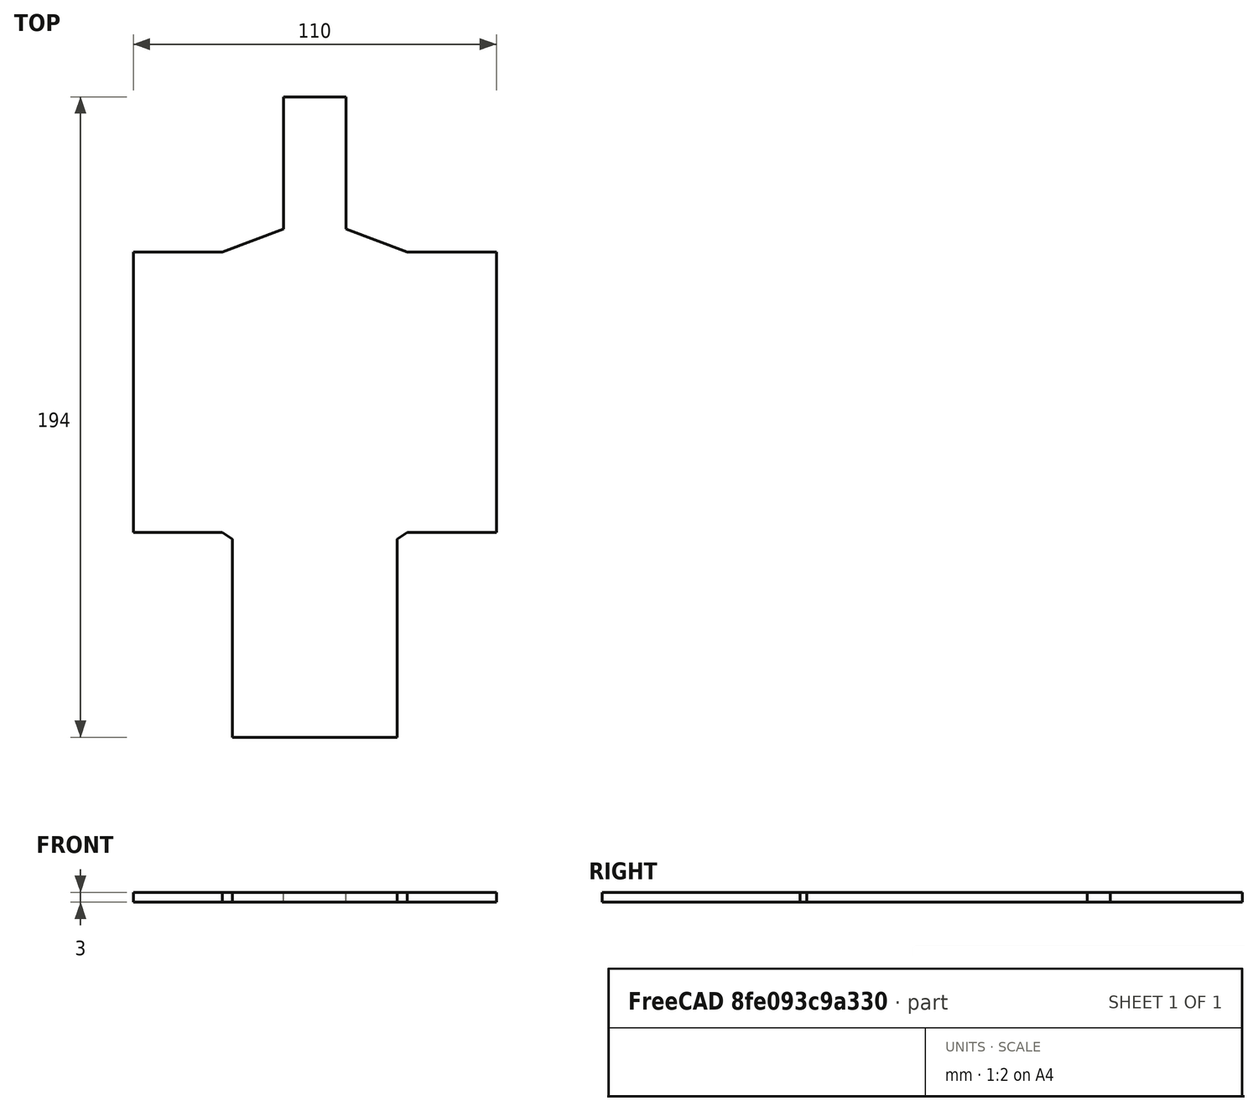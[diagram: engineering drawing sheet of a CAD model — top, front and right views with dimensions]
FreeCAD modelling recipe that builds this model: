
FCSTD DOCUMENT  (FreeCAD 0.20R29603 (Git))
Label: thesis cart platform
License: All rights reserved
LicenseURL: http://en.wikipedia.org/wiki/All_rights_reserved
objects: Sketcher::SketchObject×2, Part::Extrusion×2, PartDesign::Body×1, Part::FeaturePython×1
note: 6 computed .brp shape members not serialized (recipe doc carries the construction recipe); baked Part::Feature solids carry a one-line shape summary decoded from their .brp

FEATURE [Sketcher::SketchObject] Sketch
  FullyConstrained = true
  MapMode = 5
  Support = -> [XY_Plane]
  sketch-geometry (97):
    g0: LineSegment StartX=-55 StartY=-72.5 StartZ=0 EndX=-55 EndY=72.5 EndZ=0
    g1: LineSegment StartX=-55 StartY=72.5 StartZ=0 EndX=55 EndY=72.5 EndZ=0
    g2: LineSegment StartX=55 StartY=72.5 StartZ=0 EndX=55 EndY=-72.5 EndZ=0
    g3: LineSegment StartX=55 StartY=-72.5 StartZ=0 EndX=-55 EndY=-72.5 EndZ=0
    g4: GeomPoint X=0 Y=0 Z=0
    g5: LineSegment StartX=-55 StartY=-47.5 StartZ=0 EndX=-28 EndY=-47.5 EndZ=0
    g6: LineSegment StartX=-28 StartY=-47.5 StartZ=0 EndX=-28 EndY=-97.5 EndZ=0
    g7: LineSegment StartX=-28 StartY=-97.5 StartZ=0 EndX=-55 EndY=-97.5 EndZ=0
    g8: LineSegment StartX=-55 StartY=-97.5 StartZ=0 EndX=-55 EndY=-47.5 EndZ=0
    g9: LineSegment StartX=55 StartY=-47.5 StartZ=0 EndX=28 EndY=-47.5 EndZ=0
    g10: LineSegment StartX=28 StartY=-47.5 StartZ=0 EndX=28 EndY=-97.5 EndZ=0
    g11: LineSegment StartX=28 StartY=-97.5 StartZ=0 EndX=55 EndY=-97.5 EndZ=0
    g12: LineSegment StartX=55 StartY=-97.5 StartZ=0 EndX=55 EndY=-47.5 EndZ=0
    g13: LineSegment StartX=-55 StartY=47.5 StartZ=0 EndX=-28 EndY=47.5 EndZ=0
    g14: LineSegment StartX=-28 StartY=47.5 StartZ=0 EndX=-28 EndY=97.5 EndZ=0
    g15: LineSegment StartX=-28 StartY=97.5 StartZ=0 EndX=-55 EndY=97.5 EndZ=0
    g16: LineSegment StartX=-55 StartY=97.5 StartZ=0 EndX=-55 EndY=47.5 EndZ=0
    g17: LineSegment StartX=55 StartY=47.5 StartZ=0 EndX=28 EndY=47.5 EndZ=0
    g18: LineSegment StartX=55 StartY=97.5 StartZ=0 EndX=55 EndY=47.5 EndZ=0
    g19: LineSegment StartX=28 StartY=97.5 StartZ=0 EndX=55 EndY=97.5 EndZ=0
    g20: LineSegment StartX=28 StartY=47.5 StartZ=0 EndX=28 EndY=97.5 EndZ=0
    g21: LineSegment StartX=-7.5 StartY=72.5 StartZ=0 EndX=-7.5 EndY=84.5 EndZ=0
    g22: LineSegment StartX=-7.5 StartY=84.5 StartZ=0 EndX=7.5 EndY=84.5 EndZ=0
    g23: LineSegment StartX=7.5 StartY=84.5 StartZ=0 EndX=7.5 EndY=72.5 EndZ=0
    g24: LineSegment StartX=7.5 StartY=72.5 StartZ=0 EndX=-7.5 EndY=72.5 EndZ=0
    g25: GeomPoint X=0 Y=78.5 Z=0
    g26: LineSegment StartX=-7.5 StartY=72.5 StartZ=0 EndX=7.5 EndY=72.5 EndZ=0
    g27: LineSegment StartX=7.5 StartY=72.5 StartZ=0 EndX=7.5 EndY=60.5 EndZ=0
    g28: LineSegment StartX=7.5 StartY=60.5 StartZ=0 EndX=-7.5 EndY=60.5 EndZ=0
    g29: LineSegment StartX=-7.5 StartY=60.5 StartZ=0 EndX=-7.5 EndY=72.5 EndZ=0
    g30: Circle CenterX=-7.5 CenterY=84.5 CenterZ=0 NormalX=0 NormalY=0 NormalZ=1 AngleXU=0 Radius=1
    g31: Circle CenterX=7.5 CenterY=84.5 CenterZ=0 NormalX=0 NormalY=0 NormalZ=1 AngleXU=0 Radius=1
    g32: Circle CenterX=-7.5 CenterY=72.5 CenterZ=0 NormalX=0 NormalY=0 NormalZ=1 AngleXU=0 Radius=1
    g33: Circle CenterX=7.5 CenterY=72.5 CenterZ=0 NormalX=0 NormalY=0 NormalZ=1 AngleXU=0 Radius=1
    g34: Circle CenterX=7.5 CenterY=60.5 CenterZ=0 NormalX=0 NormalY=0 NormalZ=1 AngleXU=0 Radius=1
    g35: Circle CenterX=-7.5 CenterY=60.5 CenterZ=0 NormalX=0 NormalY=0 NormalZ=1 AngleXU=0 Radius=1
    g36: LineSegment StartX=-9.5 StartY=49.5 StartZ=0 EndX=-9.5 EndY=89.5 EndZ=0
    g37: LineSegment StartX=-9.5 StartY=89.5 StartZ=0 EndX=9.5 EndY=89.5 EndZ=0
    g38: LineSegment StartX=9.5 StartY=89.5 StartZ=0 EndX=9.5 EndY=49.5 EndZ=0
    g39: LineSegment StartX=9.5 StartY=49.5 StartZ=0 EndX=-9.5 EndY=49.5 EndZ=0
    g40: GeomPoint X=0 Y=69.5 Z=0
    g41: Circle CenterX=0 CenterY=40.5 CenterZ=0 NormalX=0 NormalY=0 NormalZ=1 AngleXU=0 Radius=7.5
    g42: LineSegment StartX=-3 StartY=30.5 StartZ=0 EndX=-3 EndY=40.5 EndZ=0
    g43: LineSegment StartX=-3 StartY=40.5 StartZ=0 EndX=3 EndY=40.5 EndZ=0
    g44: LineSegment StartX=3 StartY=40.5 StartZ=0 EndX=3 EndY=30.5 EndZ=0
    g45: LineSegment StartX=3 StartY=30.5 StartZ=0 EndX=-3 EndY=30.5 EndZ=0
    g46: GeomPoint X=0 Y=35.5 Z=0
    g47: LineSegment StartX=-21 StartY=-96 StartZ=0 EndX=-21 EndY=-49 EndZ=0
    g48: LineSegment StartX=-21 StartY=-49 StartZ=0 EndX=21 EndY=-49 EndZ=0
    g49: LineSegment StartX=21 StartY=-49 StartZ=0 EndX=21 EndY=-96 EndZ=0
    g50: LineSegment StartX=21 StartY=-96 StartZ=0 EndX=-21 EndY=-96 EndZ=0
    g51: GeomPoint X=0 Y=-72.5 Z=0
    g52: GeomPoint X=-16 Y=-96 Z=0
    g53: GeomPoint X=16 Y=-96 Z=0
    g54: GeomPoint X=16 Y=-49 Z=0
    g55: GeomPoint X=-16 Y=-49 Z=0
    g56: Circle CenterX=-21 CenterY=-49 CenterZ=0 NormalX=0 NormalY=0 NormalZ=1 AngleXU=0 Radius=0.75
    g57: Circle CenterX=-16 CenterY=-49 CenterZ=0 NormalX=0 NormalY=0 NormalZ=1 AngleXU=0 Radius=0.75
    g58: Circle CenterX=16 CenterY=-49 CenterZ=0 NormalX=0 NormalY=0 NormalZ=1 AngleXU=0 Radius=0.75
    g59: Circle CenterX=21 CenterY=-49 CenterZ=0 NormalX=0 NormalY=0 NormalZ=1 AngleXU=0 Radius=0.75
    g60: Circle CenterX=-21 CenterY=-96 CenterZ=0 NormalX=0 NormalY=0 NormalZ=1 AngleXU=0 Radius=0.75
    g61: Circle CenterX=-16 CenterY=-96 CenterZ=0 NormalX=0 NormalY=0 NormalZ=1 AngleXU=0 Radius=0.75
    g62: Circle CenterX=16 CenterY=-96 CenterZ=0 NormalX=0 NormalY=0 NormalZ=1 AngleXU=0 Radius=0.75
    g63: Circle CenterX=21 CenterY=-96 CenterZ=0 NormalX=0 NormalY=0 NormalZ=1 AngleXU=0 Radius=0.75
    g64: LineSegment StartX=-25 StartY=-104.5 StartZ=0 EndX=-25 EndY=-44.5 EndZ=0
    g65: LineSegment StartX=-25 StartY=-44.5 StartZ=0 EndX=25 EndY=-44.5 EndZ=0
    g66: LineSegment StartX=25 StartY=-44.5 StartZ=0 EndX=25 EndY=-104.5 EndZ=0
    g67: LineSegment StartX=25 StartY=-104.5 StartZ=0 EndX=-25 EndY=-104.5 EndZ=0
    g68: GeomPoint X=0 Y=-74.5 Z=0
    g69: LineSegment StartX=-2.5 StartY=-92.5 StartZ=0 EndX=-2.5 EndY=-52.5 EndZ=0
    g70: LineSegment StartX=-2.5 StartY=-52.5 StartZ=0 EndX=12.5 EndY=-52.5 EndZ=0
    g71: LineSegment StartX=12.5 StartY=-52.5 StartZ=0 EndX=12.5 EndY=-92.5 EndZ=0
    g72: LineSegment StartX=12.5 StartY=-92.5 StartZ=0 EndX=-2.5 EndY=-92.5 EndZ=0
    g73: GeomPoint X=5 Y=-72.5 Z=0
    g74: LineSegment StartX=-25 StartY=-86 StartZ=0 EndX=-25 EndY=-59 EndZ=0
    g75: LineSegment StartX=-25 StartY=-59 StartZ=0 EndX=-12 EndY=-59 EndZ=0
    g76: LineSegment StartX=-12 StartY=-59 StartZ=0 EndX=-12 EndY=-86 EndZ=0
    g77: LineSegment StartX=-12 StartY=-86 StartZ=0 EndX=-25 EndY=-86 EndZ=0
    g78: GeomPoint X=-18.5 Y=-72.5 Z=0
    g79: LineSegment StartX=12 StartY=-86 StartZ=0 EndX=12 EndY=-59 EndZ=0
    g80: LineSegment StartX=12 StartY=-59 StartZ=0 EndX=25 EndY=-59 EndZ=0
    g81: LineSegment StartX=25 StartY=-59 StartZ=0 EndX=25 EndY=-86 EndZ=0
    g82: LineSegment StartX=25 StartY=-86 StartZ=0 EndX=12 EndY=-86 EndZ=0
    g83: GeomPoint X=18.5 Y=-72.5 Z=0
    g84: LineSegment StartX=-55 StartY=-42.5 StartZ=0 EndX=-55 EndY=42.5 EndZ=0
    g85: LineSegment StartX=-55 StartY=42.5 StartZ=0 EndX=55 EndY=42.5 EndZ=0
    g86: LineSegment StartX=55 StartY=42.5 StartZ=0 EndX=55 EndY=-42.5 EndZ=0
    g87: LineSegment StartX=55 StartY=-42.5 StartZ=0 EndX=-55 EndY=-42.5 EndZ=0
    g88: GeomPoint X=0 Y=1.8e-15 Z=0
    g89: LineSegment StartX=55 StartY=42.5 StartZ=0 EndX=28 EndY=42.5 EndZ=0
    g90: LineSegment StartX=-55 StartY=42.5 StartZ=0 EndX=-28 EndY=42.5 EndZ=0
    g91: LineSegment StartX=-55 StartY=-42.5 StartZ=0 EndX=-28 EndY=-42.5 EndZ=0
    g92: LineSegment StartX=55 StartY=-42.5 StartZ=0 EndX=28 EndY=-42.5 EndZ=0
    g93: LineSegment StartX=-28 StartY=-42.5 StartZ=0 EndX=-25 EndY=-44.5 EndZ=0
    g94: LineSegment StartX=25 StartY=-44.5 StartZ=0 EndX=28 EndY=-42.5 EndZ=0
    g95: LineSegment StartX=28 StartY=42.5 StartZ=0 EndX=9.5 EndY=49.5 EndZ=0
    g96: LineSegment StartX=-28 StartY=42.5 StartZ=0 EndX=-9.5 EndY=49.5 EndZ=0
  constraints (237):
    c: Coincident(g0,g1)
    c: Coincident(g1,g2)
    c: Coincident(g2,g3)
    c: Coincident(g3,g0)
    c: Horizontal(g1)
    c: Horizontal(g3)
    c: Vertical(g0)
    c: Vertical(g2)
    c: Symmetric(g1,g0,g4)
    c: Coincident(g4,g-1)
    c: DistanceX(g1,g1) = 110
    c: DistanceY(g0,g0) = 145
    c: Coincident(g5,g6)
    c: Coincident(g6,g7)
    c: Coincident(g7,g8)
    c: Coincident(g8,g5)
    c: Horizontal(g5)
    c: Horizontal(g7)
    c: Vertical(g6)
    c: Vertical(g8)
    c: PointOnObject(g5,g0)
    c: DistanceY(g8,g8) = 50  'wheeldiam'
    c: DistanceX(g5,g5) = 27  'wheelwidth'
    c: Distance(g5,g0) = 25
    c: Coincident(g9,g10)
    c: Coincident(g10,g11)
    c: Coincident(g11,g12)
    c: Coincident(g12,g9)
    c: Horizontal(g9)
    c: Horizontal(g11)
    c: Vertical(g10)
    c: Vertical(g12)
    c: Coincident(g13,g14)
    c: Coincident(g14,g15)
    c: Coincident(g15,g16)
    c: Coincident(g16,g13)
    c: Horizontal(g13)
    c: Horizontal(g15)
    c: Vertical(g14)
    c: Vertical(g16)
    c: Coincident(g17,g20)
    c: Coincident(g20,g19)
    c: Coincident(g19,g18)
    c: Coincident(g18,g17)
    c: Horizontal(g17)
    c: Horizontal(g19)
    c: Vertical(g20)
    c: Vertical(g18)
    c: Equal(g11,g5)
    c: Equal(g6,g10)
    c: Equal(g6,g14)
    c: Equal(g5,g13)
    c: Equal(g6,g20)
    c: Equal(g5,g17)
    c: PointOnObject(g13,g0)
    c: PointOnObject(g17,g2)
    c: PointOnObject(g9,g2)
    c: Distance(g11,g2) = 25
    c: Distance(g17,g1) = 25
    c: Distance(g13,g0) = 25
    c: Coincident(g21,g22)
    c: Coincident(g22,g23)
    c: Coincident(g23,g24)
    c: Coincident(g24,g21)
    c: Horizontal(g22)
    c: Horizontal(g24)
    c: Vertical(g21)
    c: Vertical(g23)
    c: Symmetric(g22,g21,g25)
    c: Distance(g22) = 15
    c: Distance(g23) = 12
    c: Coincident(g26,g27)
    c: Coincident(g27,g28)
    c: Coincident(g28,g29)
    c: Coincident(g29,g26)
    c: Horizontal(g26)
    c: Horizontal(g28)
    c: Vertical(g27)
    c: Vertical(g29)
    c: Coincident(g26,g21)
    c: PointOnObject(g23,g27)
    c: Distance(g27) = 12
    c: PointOnObject(g21,g1)
    c: PointOnObject(g25,g-2)
    c: Coincident(g30,g21)
    c: Coincident(g31,g22)
    c: Coincident(g32,g21)
    c: Coincident(g33,g23)
    c: Coincident(g34,g27)
    c: Coincident(g35,g28)
    c: Equal(g30, g31-g35) x5
    c: Radius(g30) = 1
    c: Coincident(g36,g37)
    c: Coincident(g37,g38)
    c: Coincident(g38,g39)
    c: Coincident(g39,g36)
    c: Horizontal(g37)
    c: Horizontal(g39)
    c: Vertical(g36)
    c: Vertical(g38)
    c: Symmetric(g37,g36,g40)
    c: Distance(g37) = 19
    c: Distance(g38) = 40
    c: PointOnObject(g40,g-2)
    c: DistanceY(g30,g36) = 5
    c: Diameter(g41) = 15
    c: DistanceY(g41,g0) = 32
    c: PointOnObject(g41,g-2)
    c: Coincident(g42,g43)
    c: Coincident(g43,g44)
    c: Coincident(g44,g45)
    c: Coincident(g45,g42)
    c: Horizontal(g43)
    c: Horizontal(g45)
    c: Vertical(g42)
    c: Vertical(g44)
    c: Symmetric(g43,g42,g46)
    c: Horizontal(g42,g41)
    c: Distance(g43) = 6
    c: Distance(g42) = 10
    c: PointOnObject(g46,g-2)
    c: Coincident(g47,g48)
    c: Coincident(g48,g49)
    c: Coincident(g49,g50)
    c: Coincident(g50,g47)
    c: Horizontal(g48)
    c: Horizontal(g50)
    c: Vertical(g47)
    c: Vertical(g49)
    c: Symmetric(g48,g47,g51)
    c: DistanceX(g50,g50) = 42
    c: PointOnObject(g52,g50)
    c: PointOnObject(g53,g50)
    c: PointOnObject(g54,g48)
    c: PointOnObject(g55,g48)
    c: Vertical(g55,g52)
    c: Vertical(g54,g53)
    c: DistanceX(g47,g52) = 5
    c: DistanceX(g53,g49) = 5
    c: DistanceY(g47,g47) = 47
    c: PointOnObject(g51,g3)
    c: PointOnObject(g51,g-2)
    c: Coincident(g56,g47)
    c: Coincident(g57,g55)
    c: Coincident(g58,g54)
    c: Coincident(g59,g48)
    c: Coincident(g60,g47)
    c: Coincident(g61,g52)
    c: Coincident(g62,g53)
    c: Coincident(g63,g49)
    c: Equal(g56, g57-g63) x7
    c: Diameter(g56) = 1.5
    c: Coincident(g64,g65)
    c: Coincident(g65,g66)
    c: Coincident(g66,g67)
    c: Coincident(g67,g64)
    c: Horizontal(g65)
    c: Horizontal(g67)
    c: Vertical(g64)
    c: Vertical(g66)
    c: Symmetric(g65,g64,g68)
    c: DistanceX(g67,g67) = 50
    c: DistanceY(g64,g64) = 60
    c: DistanceY(g68,g5) = 27
    c: PointOnObject(g68,g-2)
    c: Coincident(g69,g70)
    c: Coincident(g70,g71)
    c: Coincident(g71,g72)
    c: Coincident(g72,g69)
    c: Horizontal(g70)
    c: Horizontal(g72)
    c: Vertical(g69)
    c: Vertical(g71)
    c: Symmetric(g70,g69,g73)
    c: DistanceY(g69,g69) = 40
    c: DistanceX(g72,g72) = 15
    c: PointOnObject(g73,g3)
    c: DistanceX(g73,g66) = 20
    c: Coincident(g74,g75)
    c: Coincident(g75,g76)
    c: Coincident(g76,g77)
    c: Coincident(g77,g74)
    c: Horizontal(g75)
    c: Horizontal(g77)
    c: Vertical(g74)
    c: Vertical(g76)
    c: Symmetric(g75,g74,g78)
    c: DistanceX(g77,g77) = 13
    c: DistanceY(g74,g74) = 27
    c: PointOnObject(g78,g3)
    c: Coincident(g79,g80)
    c: Coincident(g80,g81)
    c: Coincident(g81,g82)
    c: Coincident(g82,g79)
    c: Horizontal(g80)
    c: Horizontal(g82)
    c: Vertical(g79)
    c: Vertical(g81)
    c: Symmetric(g80,g79,g83)
    c: DistanceX(g82,g82) = 13
    c: DistanceY(g79,g79) = 27
    c: PointOnObject(g83,g3)
    c: PointOnObject(g74,g64)
    c: PointOnObject(g80,g66)
    c: Coincident(g84,g85)
    c: Coincident(g85,g86)
    c: Coincident(g86,g87)
    c: Coincident(g87,g84)
    c: Horizontal(g85)
    c: Horizontal(g87)
    c: Vertical(g84)
    c: Vertical(g86)
    c: Symmetric(g85,g84,g88)
    c: PointOnObject(g84,g0)
    c: PointOnObject(g88,g-2)
    c: DistanceY(g85,g17) = 5
    c: DistanceY(g9,g86) = 5
    c: Coincident(g89,g86)
    c: Coincident(g90,g84)
    c: Coincident(g91,g84)
    c: Coincident(g92,g86)
    c: Vertical(g89,g92)
    c: Vertical(g91,g90)
    c: Horizontal(g90,g89)
    c: Horizontal(g92,g91)
    c: Vertical(g90,g13)
    c: Vertical(g89,g17)
    c: PointOnObject(g89,g85)
    c: PointOnObject(g92,g87)
    c: Coincident(g93,g91)
    c: Coincident(g93,g64)
    c: Coincident(g94,g66)
    c: Coincident(g94,g92)
    c: Coincident(g95,g89)
    c: Coincident(g95,g38)
    c: Coincident(g96,g90)
    c: Coincident(g96,g36)
FEATURE [PartDesign::Body] Body
  Group = -> [Sketch]
  Origin = -> Origin
FEATURE [Sketcher::SketchObject] Sketch001
  FullyConstrained = true
  MapMode = 5
  Support = -> [XY_Plane001]
  sketch-geometry (236):
    g0: LineSegment StartX=-55 StartY=-72.5 StartZ=0 EndX=-55 EndY=72.5 EndZ=0
    g1: LineSegment StartX=-55 StartY=72.5 StartZ=0 EndX=55 EndY=72.5 EndZ=0
    g2: LineSegment StartX=55 StartY=72.5 StartZ=0 EndX=55 EndY=-72.5 EndZ=0
    g3: LineSegment StartX=55 StartY=-72.5 StartZ=0 EndX=-55 EndY=-72.5 EndZ=0
    g4: GeomPoint X=0 Y=0 Z=0
    g5: LineSegment StartX=-55 StartY=-47.5 StartZ=0 EndX=-28 EndY=-47.5 EndZ=0
    g6: LineSegment StartX=-28 StartY=-47.5 StartZ=0 EndX=-28 EndY=-97.5 EndZ=0
    g7: LineSegment StartX=-28 StartY=-97.5 StartZ=0 EndX=-55 EndY=-97.5 EndZ=0
    g8: LineSegment StartX=-55 StartY=-97.5 StartZ=0 EndX=-55 EndY=-47.5 EndZ=0
    g9: LineSegment StartX=55 StartY=-47.5 StartZ=0 EndX=28 EndY=-47.5 EndZ=0
    g10: LineSegment StartX=28 StartY=-47.5 StartZ=0 EndX=28 EndY=-97.5 EndZ=0
    g11: LineSegment StartX=28 StartY=-97.5 StartZ=0 EndX=55 EndY=-97.5 EndZ=0
    g12: LineSegment StartX=55 StartY=-97.5 StartZ=0 EndX=55 EndY=-47.5 EndZ=0
    g13: LineSegment StartX=-55 StartY=47.5 StartZ=0 EndX=-28 EndY=47.5 EndZ=0
    g14: LineSegment StartX=-28 StartY=47.5 StartZ=0 EndX=-28 EndY=97.5 EndZ=0
    g15: LineSegment StartX=-28 StartY=97.5 StartZ=0 EndX=-55 EndY=97.5 EndZ=0
    g16: LineSegment StartX=-55 StartY=97.5 StartZ=0 EndX=-55 EndY=47.5 EndZ=0
    g17: LineSegment StartX=55 StartY=47.5 StartZ=0 EndX=28 EndY=47.5 EndZ=0
    g18: LineSegment StartX=55 StartY=97.5 StartZ=0 EndX=55 EndY=47.5 EndZ=0
    g19: LineSegment StartX=28 StartY=97.5 StartZ=0 EndX=55 EndY=97.5 EndZ=0
    g20: LineSegment StartX=28 StartY=47.5 StartZ=0 EndX=28 EndY=97.5 EndZ=0
    g21: LineSegment StartX=-7.5 StartY=72.5 StartZ=0 EndX=-7.5 EndY=84.5 EndZ=0
    g22: LineSegment StartX=-7.5 StartY=84.5 StartZ=0 EndX=7.5 EndY=84.5 EndZ=0
    g23: LineSegment StartX=7.5 StartY=84.5 StartZ=0 EndX=7.5 EndY=72.5 EndZ=0
    g24: LineSegment StartX=7.5 StartY=72.5 StartZ=0 EndX=-7.5 EndY=72.5 EndZ=0
    g25: GeomPoint X=0 Y=78.5 Z=0
    g26: LineSegment StartX=-7.5 StartY=72.5 StartZ=0 EndX=7.5 EndY=72.5 EndZ=0
    g27: LineSegment StartX=7.5 StartY=72.5 StartZ=0 EndX=7.5 EndY=60.5 EndZ=0
    g28: LineSegment StartX=7.5 StartY=60.5 StartZ=0 EndX=-7.5 EndY=60.5 EndZ=0
    g29: LineSegment StartX=-7.5 StartY=60.5 StartZ=0 EndX=-7.5 EndY=72.5 EndZ=0
    g30: Circle CenterX=-7.5 CenterY=84.5 CenterZ=0 NormalX=0 NormalY=0 NormalZ=1 AngleXU=0 Radius=1
    g31: Circle CenterX=7.5 CenterY=84.5 CenterZ=0 NormalX=0 NormalY=0 NormalZ=1 AngleXU=0 Radius=1
    g32: Circle CenterX=-7.5 CenterY=72.5 CenterZ=0 NormalX=0 NormalY=0 NormalZ=1 AngleXU=0 Radius=1
    g33: Circle CenterX=7.5 CenterY=72.5 CenterZ=0 NormalX=0 NormalY=0 NormalZ=1 AngleXU=0 Radius=1
    g34: Circle CenterX=7.5 CenterY=60.5 CenterZ=0 NormalX=0 NormalY=0 NormalZ=1 AngleXU=0 Radius=1
    g35: Circle CenterX=-7.5 CenterY=60.5 CenterZ=0 NormalX=0 NormalY=0 NormalZ=1 AngleXU=0 Radius=1
    g36: LineSegment StartX=-9.5 StartY=49.5 StartZ=0 EndX=-9.5 EndY=89.5 EndZ=0
    g37: LineSegment StartX=-9.5 StartY=89.5 StartZ=0 EndX=9.5 EndY=89.5 EndZ=0
    g38: LineSegment StartX=9.5 StartY=89.5 StartZ=0 EndX=9.5 EndY=49.5 EndZ=0
    g39: LineSegment StartX=9.5 StartY=49.5 StartZ=0 EndX=-9.5 EndY=49.5 EndZ=0
    g40: GeomPoint X=0 Y=69.5 Z=0
    g41: Circle CenterX=0 CenterY=40.5 CenterZ=0 NormalX=0 NormalY=0 NormalZ=1 AngleXU=0 Radius=7.5
    g42: LineSegment StartX=-3 StartY=30.5 StartZ=0 EndX=-3 EndY=40.5 EndZ=0
    g43: LineSegment StartX=-3 StartY=40.5 StartZ=0 EndX=3 EndY=40.5 EndZ=0
    g44: LineSegment StartX=3 StartY=40.5 StartZ=0 EndX=3 EndY=30.5 EndZ=0
    g45: LineSegment StartX=3 StartY=30.5 StartZ=0 EndX=-3 EndY=30.5 EndZ=0
    g46: GeomPoint X=0 Y=35.5 Z=0
    g47: LineSegment StartX=-21 StartY=-96 StartZ=0 EndX=-21 EndY=-49 EndZ=0
    g48: LineSegment StartX=-21 StartY=-49 StartZ=0 EndX=21 EndY=-49 EndZ=0
    g49: LineSegment StartX=21 StartY=-49 StartZ=0 EndX=21 EndY=-96 EndZ=0
    g50: LineSegment StartX=21 StartY=-96 StartZ=0 EndX=-21 EndY=-96 EndZ=0
    g51: GeomPoint X=0 Y=-72.5 Z=0
    g52: GeomPoint X=-16 Y=-96 Z=0
    g53: GeomPoint X=16 Y=-96 Z=0
    g54: GeomPoint X=16 Y=-49 Z=0
    g55: GeomPoint X=-16 Y=-49 Z=0
    g56: Circle CenterX=-21 CenterY=-49 CenterZ=0 NormalX=0 NormalY=0 NormalZ=1 AngleXU=0 Radius=0.75
    g57: Circle CenterX=-16 CenterY=-49 CenterZ=0 NormalX=0 NormalY=0 NormalZ=1 AngleXU=0 Radius=0.75
    g58: Circle CenterX=16 CenterY=-49 CenterZ=0 NormalX=0 NormalY=0 NormalZ=1 AngleXU=0 Radius=0.75
    g59: Circle CenterX=21 CenterY=-49 CenterZ=0 NormalX=0 NormalY=0 NormalZ=1 AngleXU=0 Radius=0.75
    g60: Circle CenterX=-21 CenterY=-96 CenterZ=0 NormalX=0 NormalY=0 NormalZ=1 AngleXU=0 Radius=0.75
    g61: Circle CenterX=-16 CenterY=-96 CenterZ=0 NormalX=0 NormalY=0 NormalZ=1 AngleXU=0 Radius=0.75
    g62: Circle CenterX=16 CenterY=-96 CenterZ=0 NormalX=0 NormalY=0 NormalZ=1 AngleXU=0 Radius=0.75
    g63: Circle CenterX=21 CenterY=-96 CenterZ=0 NormalX=0 NormalY=0 NormalZ=1 AngleXU=0 Radius=0.75
    g64: LineSegment StartX=-25 StartY=-104.5 StartZ=0 EndX=-25 EndY=-44.5 EndZ=0
    g65: LineSegment StartX=-25 StartY=-44.5 StartZ=0 EndX=25 EndY=-44.5 EndZ=0
    g66: LineSegment StartX=25 StartY=-44.5 StartZ=0 EndX=25 EndY=-104.5 EndZ=0
    g67: LineSegment StartX=25 StartY=-104.5 StartZ=0 EndX=-25 EndY=-104.5 EndZ=0
    g68: GeomPoint X=0 Y=-74.5 Z=0
    g69: LineSegment StartX=-2.5 StartY=-92.5 StartZ=0 EndX=-2.5 EndY=-52.5 EndZ=0
    g70: LineSegment StartX=-2.5 StartY=-52.5 StartZ=0 EndX=12.5 EndY=-52.5 EndZ=0
    g71: LineSegment StartX=12.5 StartY=-52.5 StartZ=0 EndX=12.5 EndY=-92.5 EndZ=0
    g72: LineSegment StartX=12.5 StartY=-92.5 StartZ=0 EndX=-2.5 EndY=-92.5 EndZ=0
    g73: GeomPoint X=5 Y=-72.5 Z=0
    g74: LineSegment StartX=-25 StartY=-86 StartZ=0 EndX=-25 EndY=-59 EndZ=0
    g75: LineSegment StartX=-25 StartY=-59 StartZ=0 EndX=-12 EndY=-59 EndZ=0
    g76: LineSegment StartX=-12 StartY=-59 StartZ=0 EndX=-12 EndY=-86 EndZ=0
    g77: LineSegment StartX=-12 StartY=-86 StartZ=0 EndX=-25 EndY=-86 EndZ=0
    g78: GeomPoint X=-18.5 Y=-72.5 Z=0
    g79: LineSegment StartX=12 StartY=-86 StartZ=0 EndX=12 EndY=-59 EndZ=0
    g80: LineSegment StartX=12 StartY=-59 StartZ=0 EndX=25 EndY=-59 EndZ=0
    g81: LineSegment StartX=25 StartY=-59 StartZ=0 EndX=25 EndY=-86 EndZ=0
    g82: LineSegment StartX=25 StartY=-86 StartZ=0 EndX=12 EndY=-86 EndZ=0
    g83: GeomPoint X=18.5 Y=-72.5 Z=0
    g84: LineSegment StartX=-55 StartY=-42.5 StartZ=0 EndX=-55 EndY=42.5 EndZ=0
    g85: LineSegment StartX=-55 StartY=42.5 StartZ=0 EndX=55 EndY=42.5 EndZ=0
    g86: LineSegment StartX=55 StartY=42.5 StartZ=0 EndX=55 EndY=-42.5 EndZ=0
    g87: LineSegment StartX=55 StartY=-42.5 StartZ=0 EndX=-55 EndY=-42.5 EndZ=0
    g88: GeomPoint X=0 Y=2.4e-15 Z=0
    g89: LineSegment StartX=55 StartY=42.5 StartZ=0 EndX=28 EndY=42.5 EndZ=0
    g90: LineSegment StartX=-55 StartY=42.5 StartZ=0 EndX=-28 EndY=42.5 EndZ=0
    g91: LineSegment StartX=-55 StartY=-42.5 StartZ=0 EndX=-28 EndY=-42.5 EndZ=0
    g92: LineSegment StartX=55 StartY=-42.5 StartZ=0 EndX=28 EndY=-42.5 EndZ=0
    g93: LineSegment StartX=-28 StartY=-42.5 StartZ=0 EndX=-25 EndY=-44.5 EndZ=0
    g94: LineSegment StartX=25 StartY=-44.5 StartZ=0 EndX=28 EndY=-42.5 EndZ=0
    g95: LineSegment StartX=28 StartY=42.5 StartZ=0 EndX=9.5 EndY=49.5 EndZ=0
    g96: LineSegment StartX=-28 StartY=42.5 StartZ=0 EndX=-9.5 EndY=49.5 EndZ=0
    g97: Circle CenterX=-21 CenterY=-26 CenterZ=0 NormalX=0 NormalY=0 NormalZ=1 AngleXU=0 Radius=1
    g98: Circle CenterX=-16 CenterY=-26 CenterZ=0 NormalX=0 NormalY=0 NormalZ=1 AngleXU=0 Radius=1
    g99: Circle CenterX=16 CenterY=-26 CenterZ=0 NormalX=0 NormalY=0 NormalZ=1 AngleXU=0 Radius=1
    g100: Circle CenterX=21 CenterY=-26 CenterZ=0 NormalX=0 NormalY=0 NormalZ=1 AngleXU=0 Radius=1
    g101: Circle CenterX=-21 CenterY=-3 CenterZ=0 NormalX=0 NormalY=0 NormalZ=1 AngleXU=0 Radius=1
    g102: Circle CenterX=-16 CenterY=-3 CenterZ=0 NormalX=0 NormalY=0 NormalZ=1 AngleXU=0 Radius=1
    g103: Circle CenterX=16 CenterY=-3 CenterZ=0 NormalX=0 NormalY=0 NormalZ=1 AngleXU=0 Radius=1
    g104: Circle CenterX=21 CenterY=-3 CenterZ=0 NormalX=0 NormalY=0 NormalZ=1 AngleXU=0 Radius=1
    g105: LineSegment StartX=36 StartY=-39.1 StartZ=0 EndX=36 EndY=-5.9 EndZ=0
    g106: LineSegment StartX=36.9 StartY=-5 StartZ=0 EndX=37.1 EndY=-5 EndZ=0
    g107: LineSegment StartX=38 StartY=-5.9 StartZ=0 EndX=38 EndY=-39.1 EndZ=0
    g108: LineSegment StartX=37.1 StartY=-40 StartZ=0 EndX=36.9 EndY=-40 EndZ=0
    g109: GeomPoint X=37 Y=-22.5 Z=0
    g110: LineSegment StartX=30 StartY=-39.1 StartZ=0 EndX=30 EndY=-5.9 EndZ=0
    g111: LineSegment StartX=30.9 StartY=-5 StartZ=0 EndX=31.1 EndY=-5 EndZ=0
    g112: LineSegment StartX=32 StartY=-5.9 StartZ=0 EndX=32 EndY=-39.1 EndZ=0
    g113: LineSegment StartX=31.1 StartY=-40 StartZ=0 EndX=30.9 EndY=-40 EndZ=0
    g114: GeomPoint X=31 Y=-22.5 Z=0
    g115: ArcOfCircle CenterX=30.9 CenterY=-5.9 CenterZ=0 NormalX=0 NormalY=0 NormalZ=1 AngleXU=0 Radius=0.9 StartAngle=1.5708 EndAngle=3.14159
    g116: GeomPoint X=30 Y=-5 Z=0
    g117: ArcOfCircle CenterX=31.1 CenterY=-5.9 CenterZ=0 NormalX=0 NormalY=0 NormalZ=1 AngleXU=0 Radius=0.9 StartAngle=0 EndAngle=1.5708
    g118: GeomPoint X=32 Y=-5 Z=0
    g119: ArcOfCircle CenterX=36.9 CenterY=-5.9 CenterZ=0 NormalX=0 NormalY=0 NormalZ=1 AngleXU=0 Radius=0.9 StartAngle=1.5708 EndAngle=3.14159
    g120: GeomPoint X=36 Y=-5 Z=0
    g121: ArcOfCircle CenterX=37.1 CenterY=-5.9 CenterZ=0 NormalX=0 NormalY=0 NormalZ=1 AngleXU=0 Radius=0.9 StartAngle=0 EndAngle=1.5708
    g122: GeomPoint X=38 Y=-5 Z=0
    g123: ArcOfCircle CenterX=37.1 CenterY=-39.1 CenterZ=0 NormalX=0 NormalY=0 NormalZ=1 AngleXU=0 Radius=0.9 StartAngle=4.71239 EndAngle=6.28319
    g124: GeomPoint X=38 Y=-40 Z=0
    g125: ArcOfCircle CenterX=36.9 CenterY=-39.1 CenterZ=0 NormalX=0 NormalY=0 NormalZ=1 AngleXU=0 Radius=0.9 StartAngle=3.14159 EndAngle=4.71239
    g126: GeomPoint X=36 Y=-40 Z=0
    g127: ArcOfCircle CenterX=31.1 CenterY=-39.1 CenterZ=0 NormalX=0 NormalY=0 NormalZ=1 AngleXU=0 Radius=0.9 StartAngle=4.71239 EndAngle=6.28319
    g128: GeomPoint X=32 Y=-40 Z=0
    g129: ArcOfCircle CenterX=30.9 CenterY=-39.1 CenterZ=0 NormalX=0 NormalY=0 NormalZ=1 AngleXU=0 Radius=0.9 StartAngle=3.14159 EndAngle=4.71239
    g130: GeomPoint X=30 Y=-40 Z=0
    g131: LineSegment StartX=-60 StartY=2.5 StartZ=0 EndX=-25 EndY=2.5 EndZ=0
    g132: LineSegment StartX=-25 StartY=2.5 StartZ=0 EndX=-25 EndY=-42.5 EndZ=0
    g133: LineSegment StartX=-25 StartY=-42.5 StartZ=0 EndX=-60 EndY=-42.5 EndZ=0
    g134: LineSegment StartX=-60 StartY=-42.5 StartZ=0 EndX=-60 EndY=2.5 EndZ=0
    g135: LineSegment StartX=-25 StartY=-42.5 StartZ=0 EndX=-25 EndY=-40.5 EndZ=0
    g136: LineSegment StartX=-25 StartY=-42.5 StartZ=0 EndX=-26 EndY=-42.5 EndZ=0
    g137: LineSegment StartX=-25 StartY=2.5 StartZ=0 EndX=-26 EndY=2.5 EndZ=0
    g138: LineSegment StartX=-25 StartY=2.5 StartZ=0 EndX=-25 EndY=0.5 EndZ=0
    g139: Circle CenterX=-49.7781 CenterY=25.5087 CenterZ=0 NormalX=0 NormalY=0 NormalZ=1 AngleXU=0 Radius=0.75
    g140: LineSegment StartX=-49.7781 StartY=25.5087 StartZ=0 EndX=-39.7781 EndY=25.5087 EndZ=0
    g141: LineSegment StartX=-39.7781 StartY=25.5087 StartZ=0 EndX=-39.7781 EndY=15.5087 EndZ=0
    g142: LineSegment StartX=-39.7781 StartY=15.5087 StartZ=0 EndX=-49.7781 EndY=15.5087 EndZ=0
    g143: LineSegment StartX=-49.7781 StartY=15.5087 StartZ=0 EndX=-49.7781 EndY=25.5087 EndZ=0
    g144: Circle CenterX=-39.8225 CenterY=25.5069 CenterZ=0 NormalX=0 NormalY=0 NormalZ=1 AngleXU=0 Radius=0.75
    g145: LineSegment StartX=-49.7781 StartY=25.5087 StartZ=0 EndX=-39.8225 EndY=25.5069 EndZ=0
    g146: Circle CenterX=-29.8669 CenterY=25.5052 CenterZ=0 NormalX=0 NormalY=0 NormalZ=1 AngleXU=0 Radius=0.75
    g147: LineSegment StartX=-39.8225 StartY=25.5069 StartZ=0 EndX=-29.8669 EndY=25.5052 EndZ=0
    g148: Circle CenterX=-19.9112 CenterY=25.5035 CenterZ=0 NormalX=0 NormalY=0 NormalZ=1 AngleXU=0 Radius=0.75
    g149: LineSegment StartX=-29.8669 StartY=25.5052 StartZ=0 EndX=-19.9112 EndY=25.5035 EndZ=0
    g150: Circle CenterX=-9.95562 CenterY=25.5017 CenterZ=0 NormalX=0 NormalY=0 NormalZ=1 AngleXU=0 Radius=0.75
    g151: LineSegment StartX=-19.9112 StartY=25.5035 StartZ=0 EndX=-9.95562 EndY=25.5017 EndZ=0
    g152: Circle CenterX=0 CenterY=25.5 CenterZ=0 NormalX=0 NormalY=0 NormalZ=1 AngleXU=0 Radius=0.75
    g153: LineSegment StartX=-9.95562 StartY=25.5017 StartZ=0 EndX=0 EndY=25.5 EndZ=0
    g154: Circle CenterX=9.95562 CenterY=25.4983 CenterZ=0 NormalX=0 NormalY=0 NormalZ=1 AngleXU=0 Radius=0.75
    g155: LineSegment StartX=0 StartY=25.5 StartZ=0 EndX=9.95562 EndY=25.4983 EndZ=0
    g156: Circle CenterX=19.9112 CenterY=25.4965 CenterZ=0 NormalX=0 NormalY=0 NormalZ=1 AngleXU=0 Radius=0.75
    g157: LineSegment StartX=9.95562 StartY=25.4983 StartZ=0 EndX=19.9112 EndY=25.4965 EndZ=0
    g158: Circle CenterX=29.8669 CenterY=25.4948 CenterZ=0 NormalX=0 NormalY=0 NormalZ=1 AngleXU=0 Radius=0.75
    g159: LineSegment StartX=19.9112 StartY=25.4965 StartZ=0 EndX=29.8669 EndY=25.4948 EndZ=0
    g160: Circle CenterX=39.8225 CenterY=25.4931 CenterZ=0 NormalX=0 NormalY=0 NormalZ=1 AngleXU=0 Radius=0.75
    g161: LineSegment StartX=29.8669 StartY=25.4948 StartZ=0 EndX=39.8225 EndY=25.4931 EndZ=0
    g162: Circle CenterX=49.7781 CenterY=25.4913 CenterZ=0 NormalX=0 NormalY=0 NormalZ=1 AngleXU=0 Radius=0.75
    g163: LineSegment StartX=39.8225 StartY=25.4931 StartZ=0 EndX=49.7781 EndY=25.4913 EndZ=0
    g164: Circle CenterX=-49.7799 CenterY=15.553 CenterZ=0 NormalX=0 NormalY=0 NormalZ=1 AngleXU=0 Radius=0.75
    g165: LineSegment StartX=-49.7781 StartY=25.5087 StartZ=0 EndX=-49.7799 EndY=15.553 EndZ=0
    g166: Circle CenterX=-39.8242 CenterY=15.5513 CenterZ=0 NormalX=0 NormalY=0 NormalZ=1 AngleXU=0 Radius=0.75
    g167: LineSegment StartX=-49.7799 StartY=15.553 StartZ=0 EndX=-39.8242 EndY=15.5513 EndZ=0
    g168: Circle CenterX=-29.8686 CenterY=15.5496 CenterZ=0 NormalX=0 NormalY=0 NormalZ=1 AngleXU=0 Radius=0.75
    g169: LineSegment StartX=-39.8242 StartY=15.5513 StartZ=0 EndX=-29.8686 EndY=15.5496 EndZ=0
    g170: Circle CenterX=-19.913 CenterY=15.5478 CenterZ=0 NormalX=0 NormalY=0 NormalZ=1 AngleXU=0 Radius=0.75
    g171: LineSegment StartX=-29.8686 StartY=15.5496 StartZ=0 EndX=-19.913 EndY=15.5478 EndZ=0
    g172: Circle CenterX=-9.95736 CenterY=15.5461 CenterZ=0 NormalX=0 NormalY=0 NormalZ=1 AngleXU=0 Radius=0.75
    g173: LineSegment StartX=-19.913 StartY=15.5478 StartZ=0 EndX=-9.95736 EndY=15.5461 EndZ=0
    g174: Circle CenterX=-0.001733 CenterY=15.5444 CenterZ=0 NormalX=0 NormalY=0 NormalZ=1 AngleXU=0 Radius=0.75
    g175: LineSegment StartX=-9.95736 StartY=15.5461 StartZ=0 EndX=-0.001733 EndY=15.5444 EndZ=0
    g176: Circle CenterX=9.95389 CenterY=15.5426 CenterZ=0 NormalX=0 NormalY=0 NormalZ=1 AngleXU=0 Radius=0.75
    g177: LineSegment StartX=-0.001733 StartY=15.5444 StartZ=0 EndX=9.95389 EndY=15.5426 EndZ=0
    g178: Circle CenterX=19.9095 CenterY=15.5409 CenterZ=0 NormalX=0 NormalY=0 NormalZ=1 AngleXU=0 Radius=0.75
    g179: LineSegment StartX=9.95389 StartY=15.5426 StartZ=0 EndX=19.9095 EndY=15.5409 EndZ=0
    g180: Circle CenterX=29.8651 CenterY=15.5392 CenterZ=0 NormalX=0 NormalY=0 NormalZ=1 AngleXU=0 Radius=0.75
    g181: LineSegment StartX=19.9095 StartY=15.5409 StartZ=0 EndX=29.8651 EndY=15.5392 EndZ=0
    g182: Circle CenterX=39.8208 CenterY=15.5374 CenterZ=0 NormalX=0 NormalY=0 NormalZ=1 AngleXU=0 Radius=0.75
    g183: LineSegment StartX=29.8651 StartY=15.5392 StartZ=0 EndX=39.8208 EndY=15.5374 EndZ=0
    g184: Circle CenterX=49.7764 CenterY=15.5357 CenterZ=0 NormalX=0 NormalY=0 NormalZ=1 AngleXU=0 Radius=0.75
    g185: LineSegment StartX=39.8208 StartY=15.5374 StartZ=0 EndX=49.7764 EndY=15.5357 EndZ=0
    g186: Circle CenterX=-49.7816 CenterY=5.59742 CenterZ=0 NormalX=0 NormalY=0 NormalZ=1 AngleXU=0 Radius=0.75
    g187: LineSegment StartX=-49.7799 StartY=15.553 StartZ=0 EndX=-49.7816 EndY=5.59742 EndZ=0
    g188: Circle CenterX=-39.826 CenterY=5.59568 CenterZ=0 NormalX=0 NormalY=0 NormalZ=1 AngleXU=0 Radius=0.75
    g189: LineSegment StartX=-49.7816 StartY=5.59742 StartZ=0 EndX=-39.826 EndY=5.59568 EndZ=0
    g190: Circle CenterX=-29.8703 CenterY=5.59395 CenterZ=0 NormalX=0 NormalY=0 NormalZ=1 AngleXU=0 Radius=0.75
    g191: LineSegment StartX=-39.826 StartY=5.59568 StartZ=0 EndX=-29.8703 EndY=5.59395 EndZ=0
    g192: Circle CenterX=-19.9147 CenterY=5.59222 CenterZ=0 NormalX=0 NormalY=0 NormalZ=1 AngleXU=0 Radius=0.75
    g193: LineSegment StartX=-29.8703 StartY=5.59395 StartZ=0 EndX=-19.9147 EndY=5.59222 EndZ=0
    g194: Circle CenterX=-9.95909 CenterY=5.59049 CenterZ=0 NormalX=0 NormalY=0 NormalZ=1 AngleXU=0 Radius=0.75
    g195: LineSegment StartX=-19.9147 StartY=5.59222 StartZ=0 EndX=-9.95909 EndY=5.59049 EndZ=0
    g196: Circle CenterX=-0.003466 CenterY=5.58875 CenterZ=0 NormalX=0 NormalY=0 NormalZ=1 AngleXU=0 Radius=0.75
    g197: LineSegment StartX=-9.95909 StartY=5.59049 StartZ=0 EndX=-0.003466 EndY=5.58875 EndZ=0
    g198: Circle CenterX=9.95216 CenterY=5.58702 CenterZ=0 NormalX=0 NormalY=0 NormalZ=1 AngleXU=0 Radius=0.75
    g199: LineSegment StartX=-0.003466 StartY=5.58875 StartZ=0 EndX=9.95216 EndY=5.58702 EndZ=0
    g200: Circle CenterX=19.9078 CenterY=5.58529 CenterZ=0 NormalX=0 NormalY=0 NormalZ=1 AngleXU=0 Radius=0.75
    g201: LineSegment StartX=9.95216 StartY=5.58702 StartZ=0 EndX=19.9078 EndY=5.58529 EndZ=0
    g202: Circle CenterX=29.8634 CenterY=5.58355 CenterZ=0 NormalX=0 NormalY=0 NormalZ=1 AngleXU=0 Radius=0.75
    g203: LineSegment StartX=19.9078 StartY=5.58529 StartZ=0 EndX=29.8634 EndY=5.58355 EndZ=0
    g204: Circle CenterX=39.819 CenterY=5.58182 CenterZ=0 NormalX=0 NormalY=0 NormalZ=1 AngleXU=0 Radius=0.75
    g205: LineSegment StartX=29.8634 StartY=5.58355 StartZ=0 EndX=39.819 EndY=5.58182 EndZ=0
    g206: Circle CenterX=49.7747 CenterY=5.58009 CenterZ=0 NormalX=0 NormalY=0 NormalZ=1 AngleXU=0 Radius=0.75
    g207: LineSegment StartX=39.819 StartY=5.58182 StartZ=0 EndX=49.7747 EndY=5.58009 EndZ=0
    g208: LineSegment StartX=-55 StartY=-174.5 StartZ=0 EndX=-55 EndY=-104.5 EndZ=0
    g209: LineSegment StartX=-55 StartY=-104.5 StartZ=0 EndX=55 EndY=-104.5 EndZ=0
    g210: LineSegment StartX=55 StartY=-104.5 StartZ=0 EndX=55 EndY=-174.5 EndZ=0
    g211: LineSegment StartX=55 StartY=-174.5 StartZ=0 EndX=-55 EndY=-174.5 EndZ=0
    g212: GeomPoint X=7.7e-15 Y=-139.5 Z=0
    g213: LineSegment StartX=-55 StartY=-104.5 StartZ=0 EndX=-25 EndY=-104.5 EndZ=0
    g214: LineSegment StartX=55 StartY=-104.5 StartZ=0 EndX=25 EndY=-104.5 EndZ=0
    g215: LineSegment StartX=-52 StartY=-111.5 StartZ=0 EndX=-3 EndY=-111.5 EndZ=0
    g216: LineSegment StartX=-3 StartY=-111.5 StartZ=0 EndX=-3 EndY=-169.5 EndZ=0
    g217: LineSegment StartX=-3 StartY=-169.5 StartZ=0 EndX=-52 EndY=-169.5 EndZ=0
    g218: LineSegment StartX=-52 StartY=-169.5 StartZ=0 EndX=-52 EndY=-111.5 EndZ=0
    g219: Circle CenterX=-52 CenterY=-111.5 CenterZ=0 NormalX=0 NormalY=0 NormalZ=1 AngleXU=0 Radius=1.25
    g220: Circle CenterX=-3 CenterY=-111.5 CenterZ=0 NormalX=0 NormalY=0 NormalZ=1 AngleXU=0 Radius=1.25
    g221: Circle CenterX=-52 CenterY=-169.5 CenterZ=0 NormalX=0 NormalY=0 NormalZ=1 AngleXU=0 Radius=1.25
    g222: Circle CenterX=-3 CenterY=-169.5 CenterZ=0 NormalX=0 NormalY=0 NormalZ=1 AngleXU=0 Radius=1.25
    g223: Circle CenterX=19 CenterY=-111.5 CenterZ=0 NormalX=0 NormalY=0 NormalZ=1 AngleXU=0 Radius=1.25
    g224: Circle CenterX=46.9 CenterY=-111.5 CenterZ=0 NormalX=0 NormalY=0 NormalZ=1 AngleXU=0 Radius=1.25
    g225: Circle CenterX=52 CenterY=-163.6 CenterZ=0 NormalX=0 NormalY=0 NormalZ=1 AngleXU=0 Radius=1.25
    g226: Circle CenterX=3.8 CenterY=-162.3 CenterZ=0 NormalX=0 NormalY=0 NormalZ=1 AngleXU=0 Radius=1.25
    g227: LineSegment StartX=-50 StartY=-37.5 StartZ=0 EndX=-50 EndY=37.5 EndZ=0
    g228: LineSegment StartX=-50 StartY=37.5 StartZ=0 EndX=50 EndY=37.5 EndZ=0
    g229: LineSegment StartX=50 StartY=37.5 StartZ=0 EndX=50 EndY=-37.5 EndZ=0
    g230: LineSegment StartX=50 StartY=-37.5 StartZ=0 EndX=-50 EndY=-37.5 EndZ=0
    g231: GeomPoint X=0 Y=-1e-16 Z=0
    g232: Circle CenterX=-50 CenterY=37.5 CenterZ=0 NormalX=0 NormalY=0 NormalZ=1 AngleXU=0 Radius=0.75
    g233: Circle CenterX=50 CenterY=37.5 CenterZ=0 NormalX=0 NormalY=0 NormalZ=1 AngleXU=0 Radius=0.75
    g234: Circle CenterX=50 CenterY=-37.5 CenterZ=0 NormalX=0 NormalY=0 NormalZ=1 AngleXU=0 Radius=0.75
    g235: Circle CenterX=-50 CenterY=-37.5 CenterZ=0 NormalX=0 NormalY=0 NormalZ=1 AngleXU=0 Radius=0.75
  constraints (589):
    c: Coincident(g0,g1)
    c: Coincident(g1,g2)
    c: Coincident(g2,g3)
    c: Coincident(g3,g0)
    c: Horizontal(g1)
    c: Horizontal(g3)
    c: Vertical(g0)
    c: Vertical(g2)
    c: Symmetric(g1,g0,g4)
    c: Coincident(g4,g-1)
    c: DistanceX(g1,g1) = 110
    c: DistanceY(g0,g0) = 145
    c: Coincident(g5,g6)
    c: Coincident(g6,g7)
    c: Coincident(g7,g8)
    c: Coincident(g8,g5)
    c: Horizontal(g5)
    c: Horizontal(g7)
    c: Vertical(g6)
    c: Vertical(g8)
    c: PointOnObject(g5,g0)
    c: DistanceY(g8,g8) = 50  'wheeldiam'
    c: DistanceX(g5,g5) = 27  'wheelwidth'
    c: Distance(g5,g0) = 25
    c: Coincident(g9,g10)
    c: Coincident(g10,g11)
    c: Coincident(g11,g12)
    c: Coincident(g12,g9)
    c: Horizontal(g9)
    c: Horizontal(g11)
    c: Vertical(g10)
    c: Vertical(g12)
    c: Coincident(g13,g14)
    c: Coincident(g14,g15)
    c: Coincident(g15,g16)
    c: Coincident(g16,g13)
    c: Horizontal(g13)
    c: Horizontal(g15)
    c: Vertical(g14)
    c: Vertical(g16)
    c: Coincident(g17,g20)
    c: Coincident(g20,g19)
    c: Coincident(g19,g18)
    c: Coincident(g18,g17)
    c: Horizontal(g17)
    c: Horizontal(g19)
    c: Vertical(g20)
    c: Vertical(g18)
    c: Equal(g11,g5)
    c: Equal(g6,g10)
    c: Equal(g6,g14)
    c: Equal(g5,g13)
    c: Equal(g6,g20)
    c: Equal(g5,g17)
    c: PointOnObject(g13,g0)
    c: PointOnObject(g17,g2)
    c: PointOnObject(g9,g2)
    c: Distance(g11,g2) = 25
    c: Distance(g17,g1) = 25
    c: Distance(g13,g0) = 25
    c: Coincident(g21,g22)
    c: Coincident(g22,g23)
    c: Coincident(g23,g24)
    c: Coincident(g24,g21)
    c: Horizontal(g22)
    c: Horizontal(g24)
    c: Vertical(g21)
    c: Vertical(g23)
    c: Symmetric(g22,g21,g25)
    c: Distance(g22) = 15
    c: Distance(g23) = 12
    c: Coincident(g26,g27)
    c: Coincident(g27,g28)
    c: Coincident(g28,g29)
    c: Coincident(g29,g26)
    c: Horizontal(g26)
    c: Horizontal(g28)
    c: Vertical(g27)
    c: Vertical(g29)
    c: Coincident(g26,g21)
    c: PointOnObject(g23,g27)
    c: Distance(g27) = 12
    c: PointOnObject(g21,g1)
    c: PointOnObject(g25,g-2)
    c: Coincident(g30,g21)
    c: Coincident(g31,g22)
    c: Coincident(g32,g21)
    c: Coincident(g33,g23)
    c: Coincident(g34,g27)
    c: Coincident(g35,g28)
    c: Equal(g30, g31-g35) x5
    c: Radius(g30) = 1
    c: Coincident(g36,g37)
    c: Coincident(g37,g38)
    c: Coincident(g38,g39)
    c: Coincident(g39,g36)
    c: Horizontal(g37)
    c: Horizontal(g39)
    c: Vertical(g36)
    c: Vertical(g38)
    c: Symmetric(g37,g36,g40)
    c: Distance(g37) = 19
    c: Distance(g38) = 40
    c: PointOnObject(g40,g-2)
    c: DistanceY(g30,g36) = 5
    c: Diameter(g41) = 15
    c: DistanceY(g41,g0) = 32
    c: PointOnObject(g41,g-2)
    c: Coincident(g42,g43)
    c: Coincident(g43,g44)
    c: Coincident(g44,g45)
    c: Coincident(g45,g42)
    c: Horizontal(g43)
    c: Horizontal(g45)
    c: Vertical(g42)
    c: Vertical(g44)
    c: Symmetric(g43,g42,g46)
    c: Horizontal(g42,g41)
    c: Distance(g43) = 6
    c: Distance(g42) = 10
    c: PointOnObject(g46,g-2)
    c: Coincident(g47,g48)
    c: Coincident(g48,g49)
    c: Coincident(g49,g50)
    c: Coincident(g50,g47)
    c: Horizontal(g48)
    c: Horizontal(g50)
    c: Vertical(g47)
    c: Vertical(g49)
    c: Symmetric(g48,g47,g51)
    c: DistanceX(g50,g50) = 42
    c: PointOnObject(g52,g50)
    c: PointOnObject(g53,g50)
    c: PointOnObject(g54,g48)
    c: PointOnObject(g55,g48)
    c: Vertical(g55,g52)
    c: Vertical(g54,g53)
    c: DistanceX(g47,g52) = 5
    c: DistanceX(g53,g49) = 5
    c: DistanceY(g47,g47) = 47
    c: PointOnObject(g51,g3)
    c: PointOnObject(g51,g-2)
    c: Coincident(g56,g47)
    c: Coincident(g57,g55)
    c: Coincident(g58,g54)
    c: Coincident(g59,g48)
    c: Coincident(g60,g47)
    c: Coincident(g61,g52)
    c: Coincident(g62,g53)
    c: Coincident(g63,g49)
    c: Equal(g56, g57-g63) x7
    c: Diameter(g56) = 1.5
    c: Coincident(g64,g65)
    c: Coincident(g65,g66)
    c: Coincident(g66,g67)
    c: Coincident(g67,g64)
    c: Horizontal(g65)
    c: Horizontal(g67)
    c: Vertical(g64)
    c: Vertical(g66)
    c: Symmetric(g65,g64,g68)
    c: DistanceX(g67,g67) = 50
    c: DistanceY(g64,g64) = 60
    c: DistanceY(g68,g5) = 27
    c: PointOnObject(g68,g-2)
    c: Coincident(g69,g70)
    c: Coincident(g70,g71)
    c: Coincident(g71,g72)
    c: Coincident(g72,g69)
    c: Horizontal(g70)
    c: Horizontal(g72)
    c: Vertical(g69)
    c: Vertical(g71)
    c: Symmetric(g70,g69,g73)
    c: DistanceY(g69,g69) = 40
    c: DistanceX(g72,g72) = 15
    c: PointOnObject(g73,g3)
    c: DistanceX(g73,g66) = 20
    c: Coincident(g74,g75)
    c: Coincident(g75,g76)
    c: Coincident(g76,g77)
    c: Coincident(g77,g74)
    c: Horizontal(g75)
    c: Horizontal(g77)
    c: Vertical(g74)
    c: Vertical(g76)
    c: Symmetric(g75,g74,g78)
    c: DistanceX(g77,g77) = 13
    c: DistanceY(g74,g74) = 27
    c: PointOnObject(g78,g3)
    c: Coincident(g79,g80)
    c: Coincident(g80,g81)
    c: Coincident(g81,g82)
    c: Coincident(g82,g79)
    c: Horizontal(g80)
    c: Horizontal(g82)
    c: Vertical(g79)
    c: Vertical(g81)
    c: Symmetric(g80,g79,g83)
    c: DistanceX(g82,g82) = 13
    c: DistanceY(g79,g79) = 27
    c: PointOnObject(g83,g3)
    c: PointOnObject(g74,g64)
    c: PointOnObject(g80,g66)
    c: Coincident(g84,g85)
    c: Coincident(g85,g86)
    c: Coincident(g86,g87)
    c: Coincident(g87,g84)
    c: Horizontal(g85)
    c: Horizontal(g87)
    c: Vertical(g84)
    c: Vertical(g86)
    c: Symmetric(g85,g84,g88)
    c: PointOnObject(g84,g0)
    c: PointOnObject(g88,g-2)
    c: DistanceY(g85,g17) = 5
    c: DistanceY(g9,g86) = 5
    c: Coincident(g89,g86)
    c: Coincident(g90,g84)
    c: Coincident(g91,g84)
    c: Coincident(g92,g86)
    c: Vertical(g89,g92)
    c: Vertical(g91,g90)
    c: Horizontal(g90,g89)
    c: Horizontal(g92,g91)
    c: Vertical(g90,g13)
    c: Vertical(g89,g17)
    c: PointOnObject(g89,g85)
    c: PointOnObject(g92,g87)
    c: Coincident(g93,g91)
    c: Coincident(g93,g64)
    c: Coincident(g94,g66)
    c: Coincident(g94,g92)
    c: Coincident(g95,g89)
    c: Coincident(g95,g38)
    c: Coincident(g96,g90)
    c: Coincident(g96,g36)
    c: Equal(g97,g98)
    c: Equal(g97,g99)
    c: Equal(g97,g100)
    c: Diameter(g97) = 2
    c: Equal(g101,g102)
    c: Equal(g101,g103)
    c: Equal(g101,g104)
    c: Diameter(g101) = 2
    c: Vertical(g101,g97)
    c: Vertical(g102,g98)
    c: Vertical(g103,g99)
    c: Vertical(g104,g100)
    c: Horizontal(g101,g102)
    c: Horizontal(g102,g103)
    c: Horizontal(g103,g104)
    c: Horizontal(g97,g98)
    c: Horizontal(g98,g99)
    c: Horizontal(g99,g100)
    c: DistanceY(g97,g101) = 23
    c: DistanceY(g56,g97) = 23
    c: Vertical(g97,g56)
    c: Vertical(g98,g57)
    c: Vertical(g99,g58)
    c: Vertical(g100,g59)
    c: Horizontal(g106)
    c: Horizontal(g108)
    c: Vertical(g105)
    c: Vertical(g107)
    c: Symmetric(g122,g126,g109)
    c: DistanceX(g126,g124) = 2
    c: DistanceY(g126,g120) = 35
    c: Horizontal(g111)
    c: Horizontal(g113)
    c: Vertical(g110)
    c: Vertical(g112)
    c: Symmetric(g118,g130,g114)
    c: DistanceX(g130,g128) = 2
    c: DistanceY(g130,g116) = 35
    c: DistanceX(g114,g109) = 6
    c: Horizontal(g114,g109)
    c: PointOnObject(g116,g110)
    c: PointOnObject(g116,g111)
    c: Tangent(g110,g115) = 1.5708
    c: Tangent(g111,g115) = 1.5708
    c: PointOnObject(g118,g111)
    c: PointOnObject(g118,g112)
    c: Tangent(g111,g117) = 1.5708
    c: Tangent(g112,g117) = 1.5708
    c: PointOnObject(g120,g105)
    c: PointOnObject(g120,g106)
    c: Tangent(g105,g119) = 1.5708
    c: Tangent(g106,g119) = 1.5708
    c: PointOnObject(g122,g106)
    c: PointOnObject(g122,g107)
    c: Tangent(g106,g121) = 1.5708
    c: Tangent(g107,g121) = 1.5708
    c: PointOnObject(g124,g107)
    c: PointOnObject(g124,g108)
    c: Tangent(g107,g123) = 1.5708
    c: Tangent(g108,g123) = 1.5708
    c: PointOnObject(g126,g108)
    c: PointOnObject(g126,g105)
    c: Tangent(g108,g125) = 1.5708
    c: Tangent(g105,g125) = 1.5708
    c: PointOnObject(g128,g112)
    c: PointOnObject(g128,g113)
    c: Tangent(g112,g127) = 1.5708
    c: Tangent(g113,g127) = 1.5708
    c: PointOnObject(g130,g113)
    c: PointOnObject(g130,g110)
    c: Tangent(g113,g129) = 1.5708
    c: Tangent(g110,g129) = 1.5708
    c: Equal(g129,g127)
    c: Equal(g129,g125)
    c: Equal(g129,g123)
    c: Equal(g129,g121)
    c: Equal(g129,g119)
    c: Equal(g129,g117)
    c: Equal(g129,g115)
    c: Radius(g129) = 0.9
    c: DistanceY(g84,g114) = 20
    c: DistanceX(g100,g114) = 10
    c: Coincident(g131,g132)
    c: Coincident(g132,g133)
    c: Coincident(g133,g134)
    c: Coincident(g134,g131)
    c: Horizontal(g131)
    c: Horizontal(g133)
    c: Vertical(g132)
    c: Vertical(g134)
    c: DistanceY(g132,g132) = 45
    c: DistanceX(g133,g133) = 35
    c: DistanceX(g131,g84) = 5
    c: Coincident(g135,g132)
    c: Coincident(g136,g135)
    c: Coincident(g137,g131)
    c: Coincident(g138,g137)
    c: DistanceY(g138,g137) = 2
    c: DistanceX(g137,g137) = 1
    c: DistanceY(g135,g135) = 2
    c: DistanceX(g136,g135) = 1
    c: Vertical(g135,g135)
    c: Horizontal(g136,g135)
    c: Vertical(g138,g137)
    c: Horizontal(g137,g137)
    c: PointOnObject(g133,g91)
    c: Diameter(g139) = 1.5
    c: Coincident(g140,g141)
    c: Coincident(g141,g142)
    c: Coincident(g142,g143)
    c: Coincident(g143,g140)
    c: Horizontal(g140)
    c: Horizontal(g142)
    c: Vertical(g141)
    c: Vertical(g143)
    c: Coincident(g140,g139)
    c: DistanceX(g140,g140) = 10
    c: DistanceY(g143,g143) = 10
    c: Diameter(g144) = 1.5
    c: Coincident(g139,g145)
    c: Coincident(g144,g145)
    c: Distance(g145) = 9.95562
    c: Angle(g145) = -0.000174072
    c: Diameter(g146) = 1.5
    c: Coincident(g144,g147)
    c: Coincident(g146,g147)
    c: Equal(g145,g147)
    c: Parallel(g147,g145)
    c: Diameter(g148) = 1.5
    c: Coincident(g146,g149)
    c: Coincident(g148,g149)
    c: Equal(g145,g149)
    c: Parallel(g149,g145)
    c: Diameter(g150) = 1.5
    c: Coincident(g148,g151)
    c: Coincident(g150,g151)
    c: Equal(g145,g151)
    c: Parallel(g151,g145)
    c: Diameter(g152) = 1.5
    c: Coincident(g150,g153)
    c: Coincident(g152,g153)
    c: Equal(g145,g153)
    c: Parallel(g153,g145)
    c: Diameter(g154) = 1.5
    c: Coincident(g152,g155)
    c: Coincident(g154,g155)
    c: Equal(g145,g155)
    c: Parallel(g155,g145)
    c: Diameter(g156) = 1.5
    c: Coincident(g154,g157)
    c: Coincident(g156,g157)
    c: Equal(g145,g157)
    c: Parallel(g157,g145)
    c: Diameter(g158) = 1.5
    c: Coincident(g156,g159)
    c: Coincident(g158,g159)
    c: Equal(g145,g159)
    c: Parallel(g159,g145)
    c: Diameter(g160) = 1.5
    c: Coincident(g158,g161)
    c: Coincident(g160,g161)
    c: Equal(g145,g161)
    c: Parallel(g161,g145)
    c: Diameter(g162) = 1.5
    c: Coincident(g160,g163)
    c: Coincident(g162,g163)
    c: Equal(g145,g163)
    c: Parallel(g163,g145)
    c: Diameter(g164) = 1.5
    c: Coincident(g139,g165)
    c: Coincident(g164,g165)
    c: Equal(g165,g145)
    c: Perpendicular(g165,g145)
    c: Diameter(g166) = 1.5
    c: Coincident(g164,g167)
    c: Coincident(g166,g167)
    c: Equal(g145,g167)
    c: Parallel(g167,g145)
    c: Diameter(g168) = 1.5
    c: Coincident(g166,g169)
    c: Coincident(g168,g169)
    c: Equal(g145,g169)
    c: Parallel(g169,g145)
    c: Diameter(g170) = 1.5
    c: Coincident(g168,g171)
    c: Coincident(g170,g171)
    c: Equal(g145,g171)
    c: Parallel(g171,g145)
    c: Diameter(g172) = 1.5
    c: Coincident(g170,g173)
    c: Coincident(g172,g173)
    c: Equal(g145,g173)
    c: Parallel(g173,g145)
    c: Diameter(g174) = 1.5
    c: Coincident(g172,g175)
    c: Coincident(g174,g175)
    c: Equal(g145,g175)
    c: Parallel(g175,g145)
    c: Diameter(g176) = 1.5
    c: Coincident(g174,g177)
    c: Coincident(g176,g177)
    c: Equal(g145,g177)
    c: Parallel(g177,g145)
    c: Diameter(g178) = 1.5
    c: Coincident(g176,g179)
    c: Coincident(g178,g179)
    c: Equal(g145,g179)
    c: Parallel(g179,g145)
    c: Diameter(g180) = 1.5
    c: Coincident(g178,g181)
    c: Coincident(g180,g181)
    c: Equal(g145,g181)
    c: Parallel(g181,g145)
    c: Diameter(g182) = 1.5
    c: Coincident(g180,g183)
    c: Coincident(g182,g183)
    c: Equal(g145,g183)
    c: Parallel(g183,g145)
    c: Diameter(g184) = 1.5
    c: Coincident(g182,g185)
    c: Coincident(g184,g185)
    c: Equal(g145,g185)
    c: Parallel(g185,g145)
    c: Diameter(g186) = 1.5
    c: Coincident(g164,g187)
    c: Coincident(g186,g187)
    c: Equal(g165,g187)
    c: Perpendicular(g187,g145)
    c: Diameter(g188) = 1.5
    c: Coincident(g186,g189)
    c: Coincident(g188,g189)
    c: Equal(g145,g189)
    c: Parallel(g189,g145)
    c: Diameter(g190) = 1.5
    c: Coincident(g188,g191)
    c: Coincident(g190,g191)
    c: Equal(g145,g191)
    c: Parallel(g191,g145)
    c: Diameter(g192) = 1.5
    c: Coincident(g190,g193)
    c: Coincident(g192,g193)
    c: Equal(g145,g193)
    c: Parallel(g193,g145)
    c: Diameter(g194) = 1.5
    c: Coincident(g192,g195)
    c: Coincident(g194,g195)
    c: Equal(g145,g195)
    c: Parallel(g195,g145)
    c: Diameter(g196) = 1.5
    c: Coincident(g194,g197)
    c: Coincident(g196,g197)
    c: Equal(g145,g197)
    c: Parallel(g197,g145)
    c: Diameter(g198) = 1.5
    c: Coincident(g196,g199)
    c: Coincident(g198,g199)
    c: Equal(g145,g199)
    c: Parallel(g199,g145)
    c: Diameter(g200) = 1.5
    c: Coincident(g198,g201)
    c: Coincident(g200,g201)
    c: Equal(g145,g201)
    c: Parallel(g201,g145)
    c: Diameter(g202) = 1.5
    c: Coincident(g200,g203)
    c: Coincident(g202,g203)
    c: Equal(g145,g203)
    c: Parallel(g203,g145)
    c: Diameter(g204) = 1.5
    c: Coincident(g202,g205)
    c: Coincident(g204,g205)
    c: Equal(g145,g205)
    c: Parallel(g205,g145)
    c: Diameter(g206) = 1.5
    c: Coincident(g204,g207)
    c: Coincident(g206,g207)
    c: Equal(g145,g207)
    c: Parallel(g207,g145)
    c: PointOnObject(g152,g-2)
    c: DistanceY(g152,g42) = 5
    c: Coincident(g208,g209)
    c: Coincident(g209,g210)
    c: Coincident(g210,g211)
    c: Coincident(g211,g208)
    c: Horizontal(g209)
    c: Horizontal(g211)
    c: Vertical(g208)
    c: Vertical(g210)
    c: Symmetric(g209,g208,g212)
    c: PointOnObject(g208,g67)
    c: DistanceY(g208,g208) = 70
    c: Vertical(g208,g84)
    c: Vertical(g209,g86)
    c: Coincident(g213,g208)
    c: Coincident(g214,g210)
    c: PointOnObject(g214,g66)
    c: PointOnObject(g213,g64)
    c: PointOnObject(g213,g67)
    c: PointOnObject(g214,g209)
    c: Coincident(g215,g216)
    c: Coincident(g216,g217)
    c: Coincident(g217,g218)
    c: Coincident(g218,g215)
    c: Horizontal(g215)
    c: Horizontal(g217)
    c: Vertical(g216)
    c: Vertical(g218)
    c: Coincident(g219,g215)
    c: Coincident(g220,g215)
    c: Coincident(g221,g217)
    c: Coincident(g222,g216)
    c: Equal(g219,g220)
    c: Equal(g219,g221)
    c: Equal(g219,g222)
    c: Diameter(g219) = 2.5
    c: DistanceY(g218,g218) = 58
    c: DistanceX(g215,g215) = 49
    c: DistanceY(g219,g208) = 7
    c: DistanceX(g208,g219) = 3
    c: Equal(g226,g223)
    c: Equal(g226,g224)
    c: Equal(g226,g225)
    c: Diameter(g226) = 2.5
    c: Horizontal(g223,g224)
    c: DistanceX(g223,g224) = 27.9
    c: DistanceX(g224,g225) = 5.1
    c: DistanceX(g226,g223) = 15.2
    c: DistanceY(g226,g223) = 50.8
    c: DistanceY(g225,g226) = 1.3
    c: Horizontal(g223,g220)
    c: DistanceX(g225,g210) = 3
    c: Coincident(g227,g228)
    c: Coincident(g228,g229)
    c: Coincident(g229,g230)
    c: Coincident(g230,g227)
    c: Horizontal(g228)
    c: Horizontal(g230)
    c: Vertical(g227)
    c: Vertical(g229)
    c: Symmetric(g228,g227,g231)
    c: DistanceY(g229,g229) = 75
    c: DistanceY(g86,g229) = 5
    c: DistanceX(g230,g230) = 100
    c: PointOnObject(g231,g-2)
    c: Coincident(g232,g227)
    c: Coincident(g233,g228)
    c: Coincident(g234,g229)
    c: Coincident(g235,g227)
    c: Equal(g232,g233)
    c: Equal(g232,g234)
    c: Equal(g232,g235)
    c: Diameter(g232) = 1.5
FEATURE [Part::Extrusion] Extrude
  Base = -> Sketch
  Dir = (0,0,1)
  DirMode = 2
  FaceMakerClass = Part::FaceMakerBullseye
  LengthFwd = 3
  LengthRev = 0
  Solid = true
  Symmetric = false
FEATURE [Part::Extrusion] Extrude001
  Base = -> Sketch001
  Dir = (0,0,1)
  DirMode = 2
  FaceMakerClass = Part::FaceMakerBullseye
  LengthFwd = 3
  LengthRev = 0
  Solid = false
  Symmetric = false
FEATURE [Part::FeaturePython] Cutout  # WARN: FeaturePython — macro-defined, semantics opaque (R4)
  Base = -> Extrude
  Tolerance = 0
  Tool = -> Extrude001
